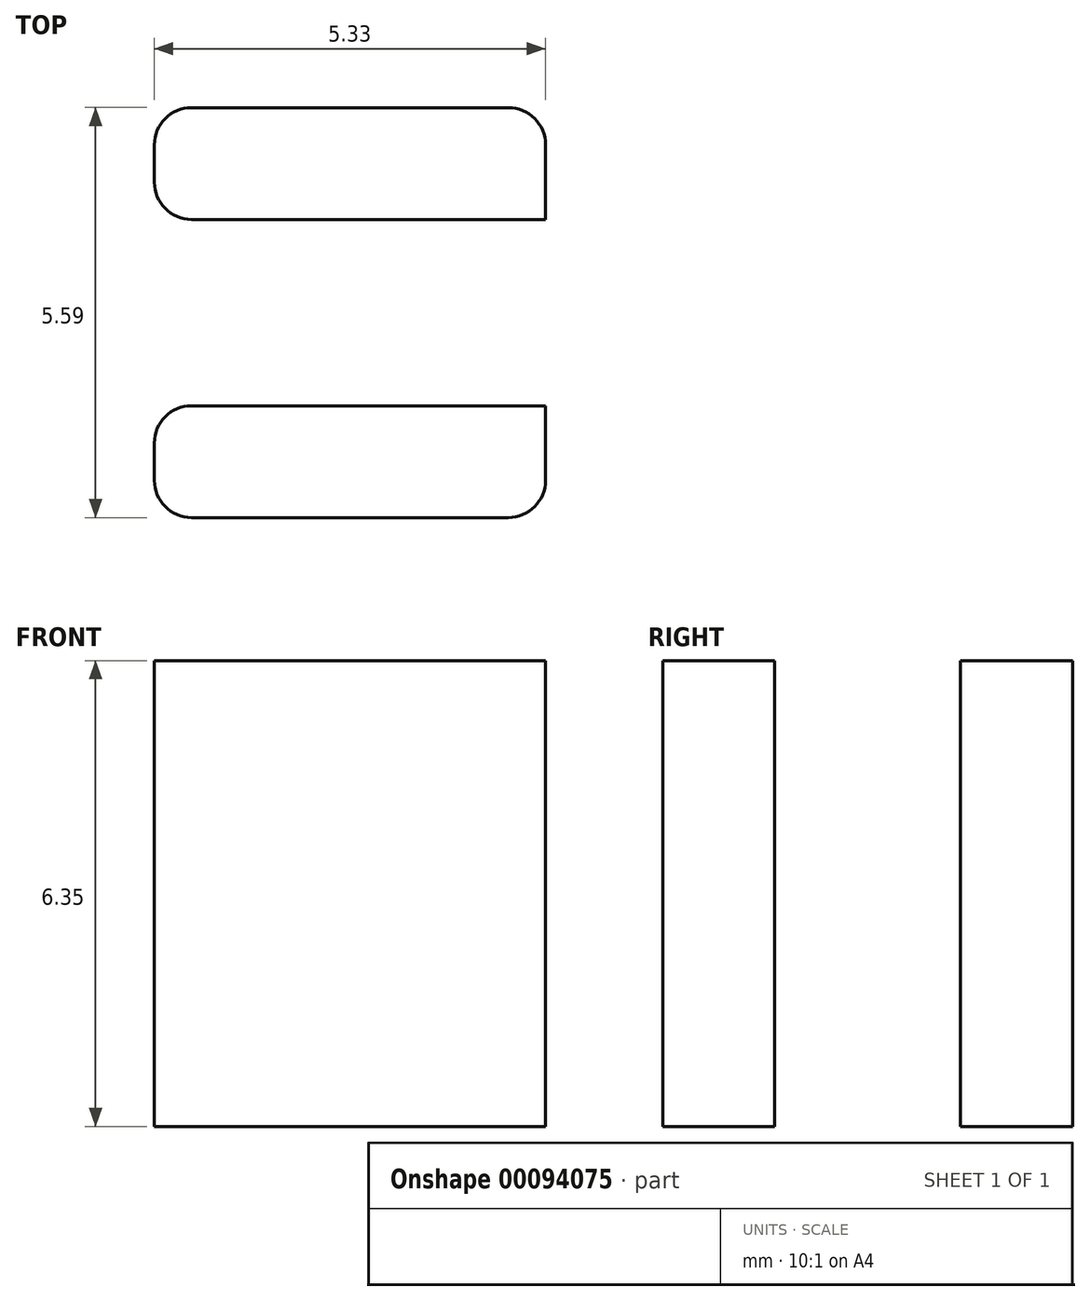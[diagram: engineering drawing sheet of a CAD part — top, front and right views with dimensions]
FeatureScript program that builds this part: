
annotation { "Feature Type Name" : "Feature", "Feature Type Description" : "" }
export const myFeature = defineFeature(function(context is Context, id is Id, definition is map)
    precondition{}
    {
        {
            var Q0;
            Q0=qCreatedBy(makeId("Top.planeOp"),FACE);
            var sketch = newSketch(context, id + "F0", { "sketchPlane" : qUnion([Q0])});
            skLineSegment(sketch, "E0.bottom", {"start": v(0, 0) * mm, "end": v(5.33, 0) * mm});
            skLineSegment(sketch, "E0.top", {"start": v(0, 1.52) * mm, "end": v(5.33, 1.52) * mm});
            skLineSegment(sketch, "E0.left", {"start": v(0, 0) * mm, "end": v(0, 1.52) * mm});
            skLineSegment(sketch, "E0.right", {"start": v(5.33, 0) * mm, "end": v(5.33, 1.52) * mm});
            skLineSegment(sketch, "E1.bottom", {"start": v(5.33, 1.52) * mm, "end": v(3.81, 1.52) * mm});
            skLineSegment(sketch, "E1.top", {"start": v(5.33, 4.06) * mm, "end": v(3.81, 4.06) * mm});
            skLineSegment(sketch, "E1.left", {"start": v(5.33, 1.52) * mm, "end": v(5.33, 4.06) * mm});
            skLineSegment(sketch, "E1.right", {"start": v(3.8, 1.52) * mm, "end": v(3.81, 4.06) * mm});
            skLineSegment(sketch, "E2.bottom", {"start": v(5.33, 4.06) * mm, "end": v(0, 4.06) * mm});
            skLineSegment(sketch, "E2.top", {"start": v(5.33, 5.59) * mm, "end": v(0, 5.59) * mm});
            skLineSegment(sketch, "E2.left", {"start": v(5.33, 4.06) * mm, "end": v(5.33, 5.59) * mm});
            skLineSegment(sketch, "E2.right", {"start": v(0, 4.06) * mm, "end": v(0, 5.59) * mm});
            skSolve(sketch);
        }
        {
            var Q0;
            Q0=makeQuery(id+"F0.imprint","IMPRINT",FACE,{"disambiguationData":[TD([[makeQuery(id+"F0.imprint","IMPRINT",EDGE,{"derivedFrom":sQuery(id+"F0.wireOp",EDGE,"E2.top")}),1.0]])]});
            var Q1;
            Q1=makeQuery(id+"F0.imprint","IMPRINT",FACE,{"disambiguationData":[TD([[makeQuery(id+"F0.imprint","IMPRINT",EDGE,{"derivedFrom":sQuery(id+"F0.wireOp",EDGE,"E1.bottom")}),-1.0]])]});
            var Q2;
            Q2=makeQuery(id+"F0.imprint","IMPRINT",FACE,{"disambiguationData":[TD([[makeQuery(id+"F0.imprint","IMPRINT",EDGE,{"derivedFrom":sQuery(id+"F0.wireOp",EDGE,"E0.bottom")}),1.0]])]});
            extrude(context, id + "F1", {"entities" : qUnion([Q0, Q1, Q2]), "depth" : 6.35 * mm, "offsetDistance" : 25.4 * mm});
        }
        {
            var Q0;
            Q0=makeQuery(id+"F1.opExtrude","SWEPT_EDGE",EDGE,{"disambiguationData":[OSD([sQuery(id+"F0.wireOp",EDGE,"E2.bottom"),sQuery(id+"F0.wireOp",EDGE,"E2.right")])]});
            var Q1;
            Q1=makeQuery(id+"F1.opExtrude","SWEPT_EDGE",EDGE,{"disambiguationData":[OSD([sQuery(id+"F0.wireOp",EDGE,"E2.top"),sQuery(id+"F0.wireOp",EDGE,"E2.right")])]});
            var Q2;
            Q2=makeQuery(id+"F1.opExtrude","SWEPT_EDGE",EDGE,{"disambiguationData":[OSD([sQuery(id+"F0.wireOp",EDGE,"E0.top"),sQuery(id+"F0.wireOp",EDGE,"E0.left")])]});
            var Q3;
            Q3=makeQuery(id+"F1.opExtrude","SWEPT_EDGE",EDGE,{"disambiguationData":[OSD([sQuery(id+"F0.wireOp",EDGE,"E0.bottom"),sQuery(id+"F0.wireOp",EDGE,"E0.left")])]});
            var Q4;
            Q4=makeQuery(id+"F1.opExtrude","SWEPT_EDGE",EDGE,{"disambiguationData":[OSD([sQuery(id+"F0.wireOp",EDGE,"E0.bottom"),sQuery(id+"F0.wireOp",EDGE,"E0.right")])]});
            var Q5;
            Q5=makeQuery(id+"F1.opExtrude","SWEPT_EDGE",EDGE,{"disambiguationData":[OSD([sQuery(id+"F0.wireOp",EDGE,"E2.top"),sQuery(id+"F0.wireOp",EDGE,"E2.left")])]});
            fillet(context, id + "F2", {"entities" : qUnion([Q0, Q1, Q2, Q3, Q4, Q5]), "radius" : 0.5 * mm, "tangentPropagation" : true, "allowEdgeOverflow" : false});
        }
    });
